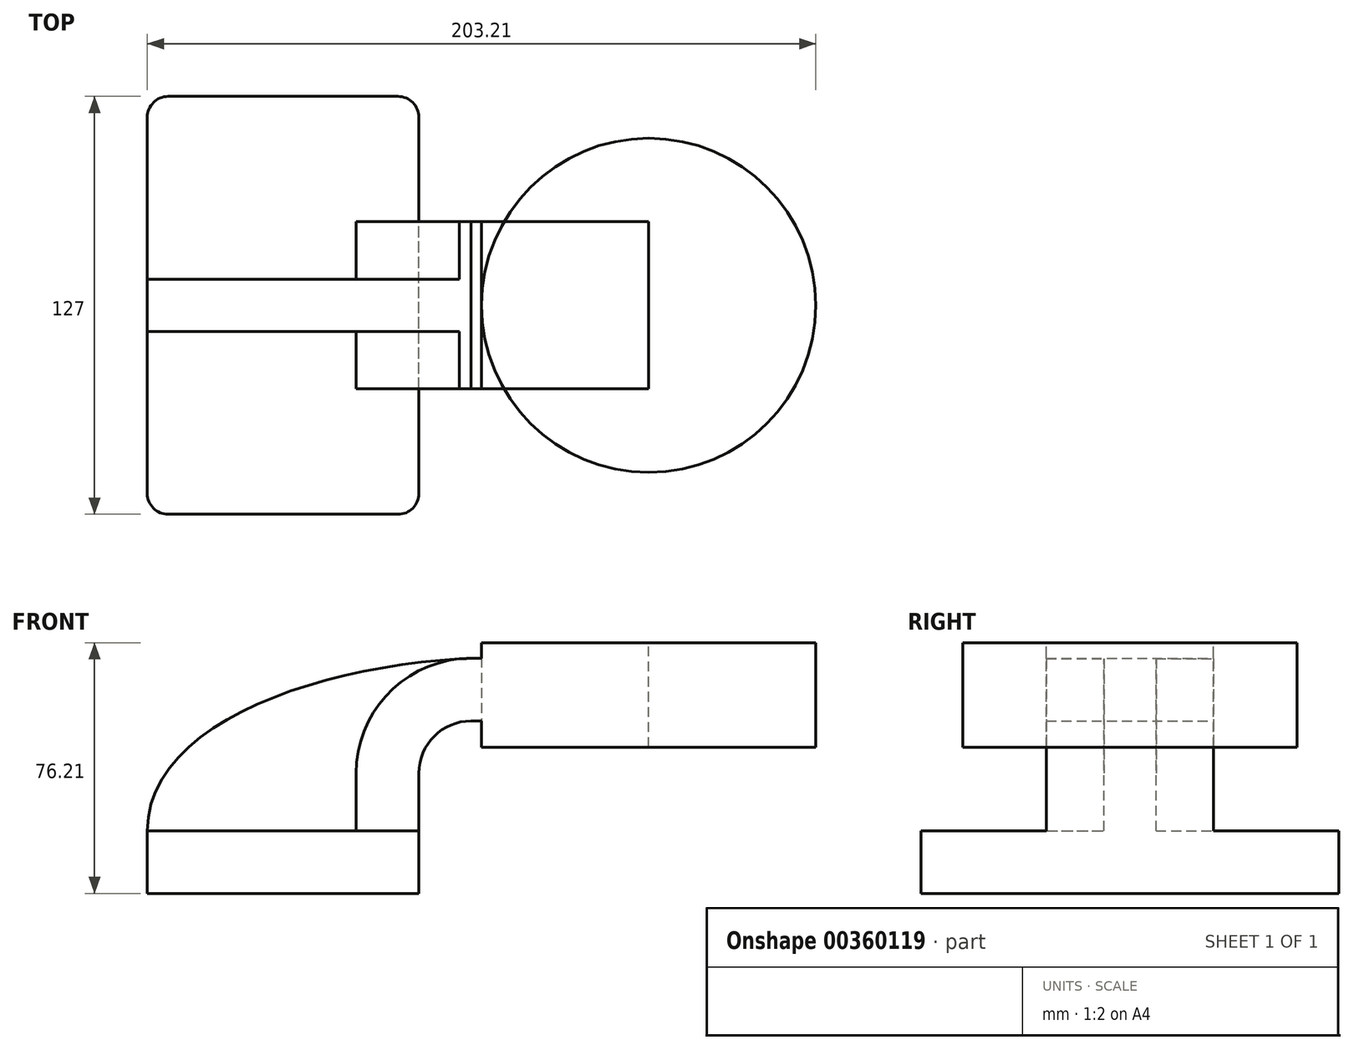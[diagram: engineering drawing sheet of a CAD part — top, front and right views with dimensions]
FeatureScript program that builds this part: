
annotation { "Feature Type Name" : "Feature", "Feature Type Description" : "" }
export const myFeature = defineFeature(function(context is Context, id is Id, definition is map)
    precondition{}
    {
        {
            var Q0;
            Q0=qCreatedBy(makeId("Front.planeOp"),FACE);
            var sketch = newSketch(context, id + "F0", { "sketchPlane" : qUnion([Q0])});
            skLineSegment(sketch, "E0.bottom", {"start": v(-41.27, -9.53) * mm, "end": v(41.28, -9.53) * mm});
            skLineSegment(sketch, "E0.top", {"start": v(-41.28, 9.52) * mm, "end": v(41.28, 9.52) * mm});
            skLineSegment(sketch, "E0.left", {"start": v(-41.28, -9.53) * mm, "end": v(-41.28, 9.53) * mm});
            skLineSegment(sketch, "E0.right", {"start": v(41.28, -9.53) * mm, "end": v(41.28, 9.52) * mm});
            skPoint(sketch, "E0.middle", {"position": v(0, 0) * mm});
            skLineSegment(sketch, "E1.bottom", {"start": v(60.33, 34.93) * mm, "end": v(111.13, 34.93) * mm});
            skLineSegment(sketch, "E1.top", {"start": v(60.33, 66.67) * mm, "end": v(111.13, 66.67) * mm});
            skLineSegment(sketch, "E1.left", {"start": v(60.33, 34.93) * mm, "end": v(60.33, 66.67) * mm});
            skLineSegment(sketch, "E1.right", {"start": v(111.13, 34.93) * mm, "end": v(111.13, 66.67) * mm});
            skPoint(sketch, "E1.middle", {"position": v(85.73, 50.8) * mm});
            skLineSegment(sketch, "E2", {"start": v(41.28, 9.52) * mm, "end": v(41.28, 27) * mm});
            skArc(sketch, "E3", {"start": v(41.27, 27) * mm, "mid": v(45.92, 38.23) * mm, "end": v(57.15, 42.88) * mm});
            skLineSegment(sketch, "E4", {"start": v(57.15, 42.88) * mm, "end": v(83.91, 42.88) * mm});
            skLineSegment(sketch, "E5.0", {"start": v(22.22, 9.52) * mm, "end": v(22.22, 27) * mm});
            skArc(sketch, "E6.0", {"start": v(22.22, 27) * mm, "mid": v(32.45, 51.7) * mm, "end": v(57.15, 61.93) * mm});
            skLineSegment(sketch, "E7", {"start": v(57.15, 61.93) * mm, "end": v(84, 61.93) * mm});
            skFitSpline(sketch, "E8", {"points": [v(-41.27, 9.52) * mm, v(57.15, 61.93) * mm], "startDerivative": vector(0.72, 100.33) * mm, "endDerivative": vector(134.29, 5.77) * mm});
            skSolve(sketch);
        }
        {
            var Q0;
            Q0=makeQuery(id+"F0.imprint","IMPRINT",FACE,{"disambiguationData":[TD([[makeQuery(id+"F0.imprint","IMPRINT",EDGE,{"derivedFrom":sQuery(id+"F0.wireOp",EDGE,"E0.bottom")}),1.0]])]});
            extrude(context, id + "F1", {"entities" : qUnion([Q0]), "endBound" : BoundingType.SYMMETRIC, "depth" : 127 * mm});
        }
        {
            var Q0;
            {var subQ0=sQuery(id+"F0.wireOp",EDGE,"E2");Q0=makeQuery(id+"F0.imprint","IMPRINT",FACE,{"disambiguationData":[TD([[makeQuery(id+"F0.imprint","IMPRINT",EDGE,{"derivedFrom":subQ0}),1.0]])]});}
            var Q1;
            {var subQ3=sQuery(id+"F0.wireOp",EDGE,"E1.bottom");Q1=makeQuery(id+"F0.imprint","IMPRINT",FACE,{"disambiguationData":[TD([[makeQuery(id+"F0.imprint","IMPRINT",EDGE,{"derivedFrom":subQ3}),1.0]])]});}
            extrude(context, id + "F2", {"entities" : qUnion([Q0, Q1]), "operationType" : NewBodyOperationType.ADD, "endBound" : BoundingType.SYMMETRIC, "depth" : 50.8 * mm});
        }
        {
            var Q0;
            {var subQ3=sQuery(id+"F0.wireOp",EDGE,"E5.0");Q0=makeQuery(id+"F0.imprint","IMPRINT",FACE,{"disambiguationData":[TD([[makeQuery(id+"F0.imprint","IMPRINT",EDGE,{"derivedFrom":subQ3}),1.0]])]});}
            extrude(context, id + "F3", {"entities" : qUnion([Q0]), "operationType" : NewBodyOperationType.ADD, "endBound" : BoundingType.SYMMETRIC, "depth" : 15.88 * mm});
        }
        {
            var Q0;
            {var subQ3=sQuery(id+"F0.wireOp",EDGE,"E1.bottom");Q0=makeQuery(id+"F0.imprint","IMPRINT",FACE,{"disambiguationData":[TD([[makeQuery(id+"F0.imprint","IMPRINT",EDGE,{"derivedFrom":subQ3}),1.0]])]});}
            var Q1;
            Q1=sQuery(id+"F0.wireOp",EDGE,"E1.right");
            revolve(context, id + "F4", {"entities" : qUnion([Q0]), "axis" : qUnion([Q1]), "revolveType" : RevolveType.FULL});
        }
        {
            var Q0;
            Q0=makeQuery(id+"F1.opExtrude","CAP_EDGE",EDGE,{"disambiguationData":[OSD([sQuery(id+"F0.wireOp",EDGE,"E0.right")])],"isStart":false});
            var Q1;
            Q1=makeQuery(id+"F1.opExtrude","CAP_EDGE",EDGE,{"disambiguationData":[OSD([sQuery(id+"F0.wireOp",EDGE,"E0.left")])],"isStart":false});
            var Q2;
            Q2=makeQuery(id+"F1.opExtrude","CAP_EDGE",EDGE,{"disambiguationData":[OSD([sQuery(id+"F0.wireOp",EDGE,"E0.right")])],"isStart":true});
            var Q3;
            Q3=makeQuery(id+"F1.opExtrude","CAP_EDGE",EDGE,{"disambiguationData":[OSD([sQuery(id+"F0.wireOp",EDGE,"E0.left")])],"isStart":true});
            fillet(context, id + "F5", {"entities" : qUnion([Q0, Q1, Q2, Q3]), "radius" : 6.35 * mm, "tangentPropagation" : true, "allowEdgeOverflow" : false});
        }
    });
